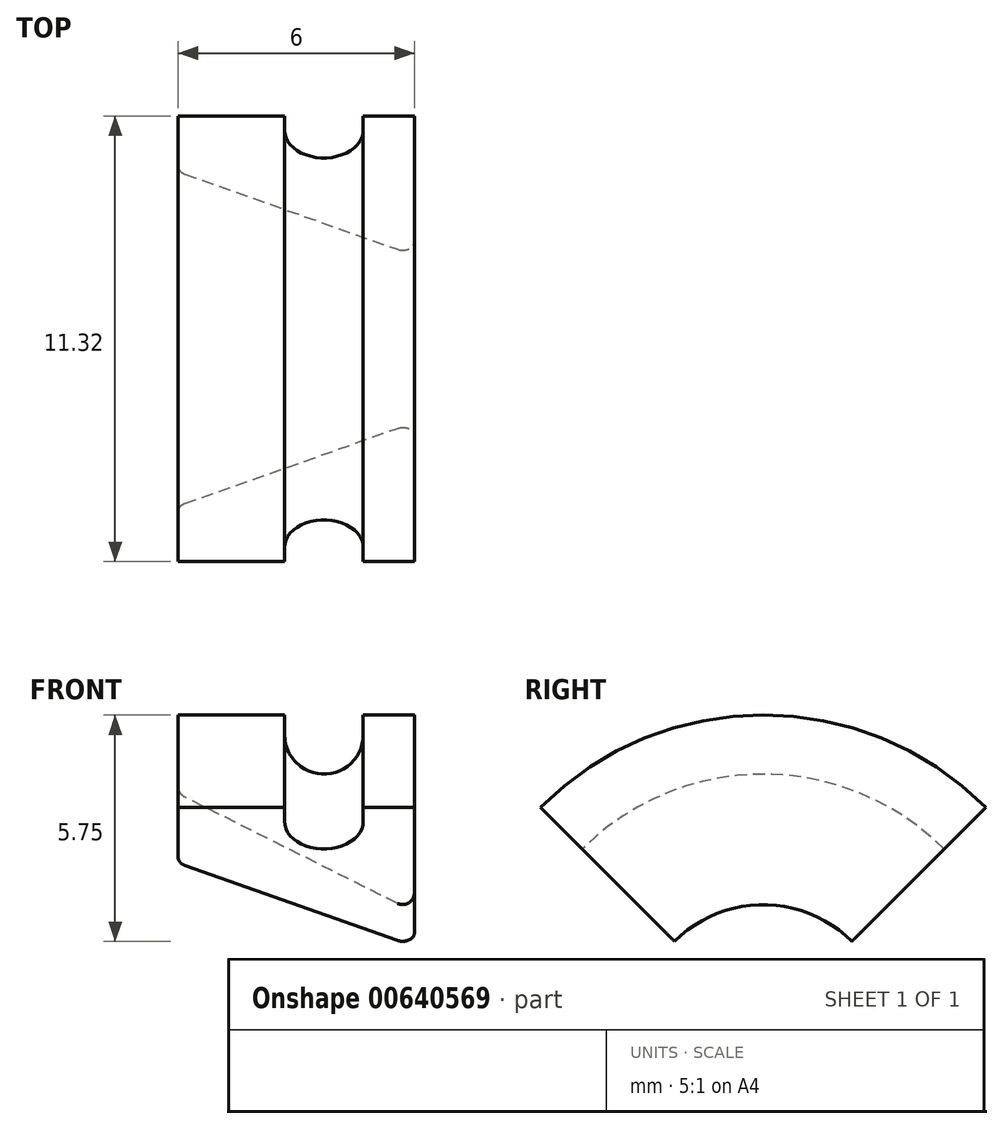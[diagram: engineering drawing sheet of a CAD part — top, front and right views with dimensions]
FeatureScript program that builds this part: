
annotation { "Feature Type Name" : "Feature", "Feature Type Description" : "" }
export const myFeature = defineFeature(function(context is Context, id is Id, definition is map)
    precondition{}
    {
        {
            var Q0;
            Q0=qCreatedBy(makeId("Front.planeOp"),FACE);
            var sketch = newSketch(context, id + "F0", { "sketchPlane" : qUnion([Q0])});
            skLineSegment(sketch, "E0", {"start": v(0, 4) * mm, "end": v(2, 3) * mm});
            skLineSegment(sketch, "E1", {"start": v(2, 3) * mm, "end": v(2, 8) * mm});
            skLineSegment(sketch, "E2", {"start": v(0, 10) * mm, "end": v(0, 4) * mm, "construction": true});
            skLineSegment(sketch, "E3", {"start": v(-3.9, 0) * mm, "end": v(6.54, 0) * mm, "construction": true});
            skLineSegment(sketch, "E4", {"start": v(0, 4) * mm, "end": v(-4, 6) * mm});
            skLineSegment(sketch, "E5", {"start": v(-4, 6) * mm, "end": v(-4, 8) * mm});
            skLineSegment(sketch, "E6", {"start": v(-4, 8) * mm, "end": v(-1.3, 8) * mm});
            skLineSegment(sketch, "E7", {"start": v(-1.3, 8) * mm, "end": v(-1.3, 7.5) * mm});
            skLineSegment(sketch, "E8", {"start": v(0.7, 7.5) * mm, "end": v(0.7, 8) * mm});
            skLineSegment(sketch, "E9", {"start": v(0.7, 8) * mm, "end": v(2, 8) * mm});
            skLineSegment(sketch, "E10", {"start": v(-0.3, 6) * mm, "end": v(-0.3, 9.92) * mm, "construction": true});
            skArc(sketch, "E11", {"start": v(-1.3, 7.5) * mm, "mid": v(-0.3, 6.5) * mm, "end": v(0.7, 7.5) * mm});
            skSolve(sketch);
        }
        {
            var Q0;
            Q0 = qSketchRegion(id + "F0", true);
            var Q1;
            Q1=sQuery(id+"F0.wireOp",EDGE,"E3");
            revolve(context, id + "F1", {"entities" : qUnion([Q0]), "axis" : qUnion([Q1]), "revolveType" : RevolveType.SYMMETRIC, "angle" : 90 * degree});
        }
        {
            var Q0;
            Q0=makeQuery(id+"F1.opRevolve","SWEPT_EDGE",EDGE,{"disambiguationData":[OSD([sQuery(id+"F0.wireOp",EDGE,"E0"),sQuery(id+"F0.wireOp",EDGE,"E1")])]});
            var Q1;
            Q1=makeQuery(id+"F1.opRevolve","SWEPT_EDGE",EDGE,{"disambiguationData":[OSD([sQuery(id+"F0.wireOp",EDGE,"E4"),sQuery(id+"F0.wireOp",EDGE,"E5")])]});
            fillet(context, id + "F2", {"entities" : qUnion([Q0, Q1]), "radius" : 0.3 * mm, "tangentPropagation" : true, "allowEdgeOverflow" : false});
        }
    });
